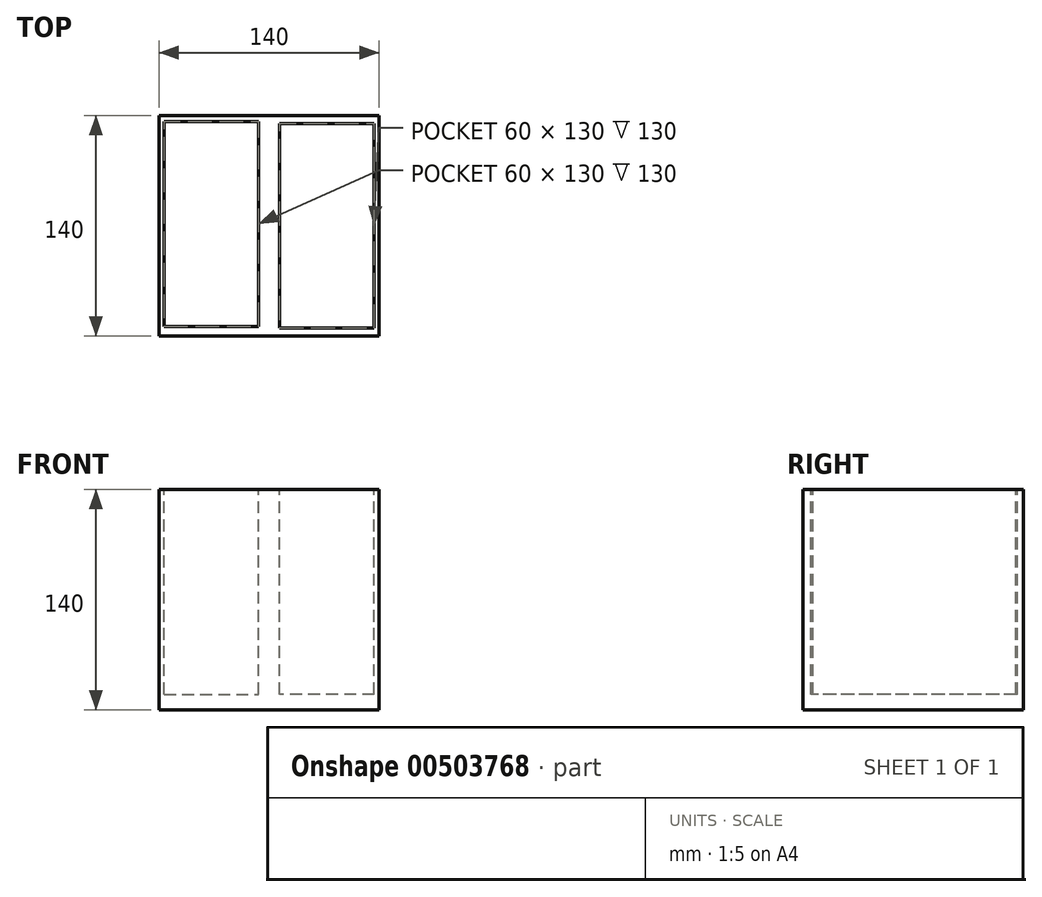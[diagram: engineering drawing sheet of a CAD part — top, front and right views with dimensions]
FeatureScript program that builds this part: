
annotation { "Feature Type Name" : "Feature", "Feature Type Description" : "" }
export const myFeature = defineFeature(function(context is Context, id is Id, definition is map)
    precondition{}
    {
        {
            var Q0;
            Q0=qCreatedBy(makeId("Top.planeOp"),FACE);
            var sketch = newSketch(context, id + "F0", { "sketchPlane" : qUnion([Q0])});
            skLineSegment(sketch, "E0.bottom", {"start": v(-70, -70) * mm, "end": v(70, -70) * mm});
            skLineSegment(sketch, "E0.top", {"start": v(-70, 70) * mm, "end": v(70, 70) * mm});
            skLineSegment(sketch, "E0.left", {"start": v(-70, -70) * mm, "end": v(-70, 70) * mm});
            skLineSegment(sketch, "E0.right", {"start": v(70, -70) * mm, "end": v(70, 70) * mm});
            skPoint(sketch, "E0.middle", {"position": v(0, 0) * mm});
            skSolve(sketch);
        }
        {
            var Q0;
            Q0=makeQuery(id+"F0.imprint","IMPRINT",FACE,{"disambiguationData":[TD([[makeQuery(id+"F0.imprint","IMPRINT",EDGE,{"derivedFrom":sQuery(id+"F0.wireOp",EDGE,"E0.bottom")}),1.0]])]});
            extrude(context, id + "F1", {"entities" : qUnion([Q0]), "depth" : 140 * mm});
        }
        {
            var Q0;
            Q0=makeQuery(id+"F1.opExtrude","CAP_FACE",FACE,{"disambiguationData":[OSD([sQuery(id+"F0.wireOp",EDGE,"E0.bottom"),sQuery(id+"F0.wireOp",EDGE,"E0.top"),sQuery(id+"F0.wireOp",EDGE,"E0.left"),sQuery(id+"F0.wireOp",EDGE,"E0.right")])],"isStart":false});
            var sketch = newSketch(context, id + "F2", { "sketchPlane" : qUnion([Q0])});
            skLineSegment(sketch, "E1.bottom", {"start": v(66.83, 65.01) * mm, "end": v(6.83, 65.01) * mm});
            skLineSegment(sketch, "E1.top", {"start": v(66.83, -64.99) * mm, "end": v(6.83, -64.99) * mm});
            skLineSegment(sketch, "E1.left", {"start": v(66.83, 65.01) * mm, "end": v(66.83, -64.99) * mm});
            skLineSegment(sketch, "E1.right", {"start": v(6.83, 65.01) * mm, "end": v(6.83, -64.99) * mm});
            skSolve(sketch);
        }
        {
            var Q0;
            Q0=makeQuery(id+"F2.imprint","IMPRINT",FACE,{"disambiguationData":[TD([[makeQuery(id+"F2.imprint","IMPRINT",EDGE,{"derivedFrom":sQuery(id+"F2.wireOp",EDGE,"E1.bottom")}),-1.0]])]});
            var sketch = newSketch(context, id + "F3", { "sketchPlane" : qUnion([Q0])});
            skLineSegment(sketch, "E2.bottom", {"start": v(-66.68, 66.19) * mm, "end": v(-6.68, 66.19) * mm});
            skLineSegment(sketch, "E2.top", {"start": v(-66.68, -63.81) * mm, "end": v(-6.68, -63.81) * mm});
            skLineSegment(sketch, "E2.left", {"start": v(-66.68, 66.19) * mm, "end": v(-66.68, -63.81) * mm});
            skLineSegment(sketch, "E2.right", {"start": v(-6.68, 66.19) * mm, "end": v(-6.68, -63.81) * mm});
            skSolve(sketch);
        }
        {
            var Q0;
            Q0=makeQuery(id+"F2.imprint","IMPRINT",FACE,{"disambiguationData":[TD([[makeQuery(id+"F2.imprint","IMPRINT",EDGE,{"derivedFrom":sQuery(id+"F2.wireOp",EDGE,"E1.bottom")}),1.0]])]});
            extrude(context, id + "F4", {"entities" : qUnion([Q0]), "operationType" : NewBodyOperationType.REMOVE, "oppositeDirection" : true, "depth" : 130 * mm});
        }
        {
            var Q0;
            Q0=makeQuery(id+"F3.imprint","IMPRINT",FACE,{"disambiguationData":[TD([[makeQuery(id+"F3.imprint","IMPRINT",EDGE,{"derivedFrom":sQuery(id+"F3.wireOp",EDGE,"E2.bottom")}),-1.0]])]});
            extrude(context, id + "F5", {"entities" : qUnion([Q0]), "operationType" : NewBodyOperationType.REMOVE, "oppositeDirection" : true, "depth" : 130 * mm});
        }
    });
